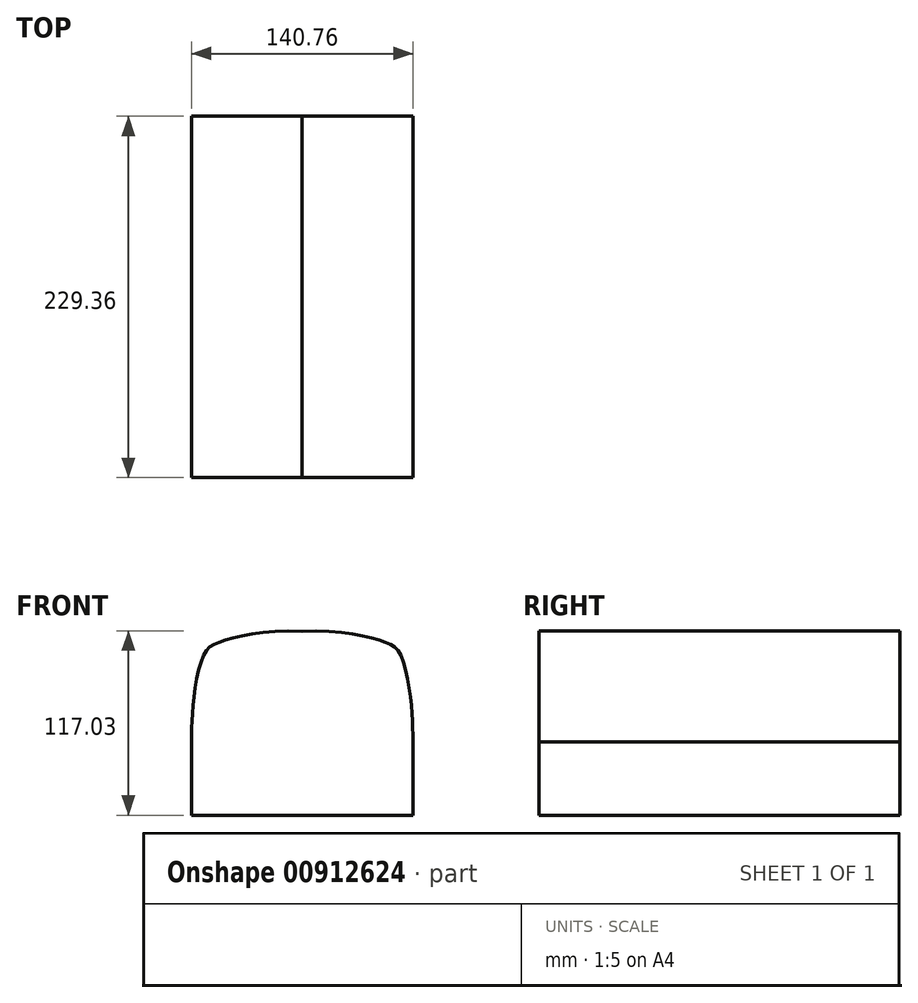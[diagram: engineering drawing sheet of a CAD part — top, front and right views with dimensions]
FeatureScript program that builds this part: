
annotation { "Feature Type Name" : "Feature", "Feature Type Description" : "" }
export const myFeature = defineFeature(function(context is Context, id is Id, definition is map)
    precondition{}
    {
        {
            var Q0;
            Q0=qCreatedBy(makeId("Front.planeOp"),FACE);
            var sketch = newSketch(context, id + "F0", { "sketchPlane" : qUnion([Q0])});
            skLineSegment(sketch, "E0", {"start": v(-70.38, -58.83) * mm, "end": v(70.38, -58.83) * mm});
            skLineSegment(sketch, "E1", {"start": v(70.38, -58.83) * mm, "end": v(70.38, -12.25) * mm});
            skLineSegment(sketch, "E2", {"start": v(-70.38, -58.83) * mm, "end": v(-70.38, -12.25) * mm});
            skFitSpline(sketch, "E3", {"points": [v(-70.38, -12.25) * mm, v(-69.1, 13) * mm, v(-61.82, 44.19) * mm, v(-51.98, 51.3) * mm, v(0, 57.92) * mm], "startDerivative": vector(3.91, 99.43) * mm, "endDerivative": vector(209.58, -13.11) * mm});
            skLineSegment(sketch, "E4", {"start": v(0, 57.92) * mm, "end": v(0, -58.83) * mm});
            skFitSpline(sketch, "E5.MirrorCS", {"points": [v(70.38, -12.25) * mm, v(69.1, 13) * mm, v(61.82, 44.19) * mm, v(51.98, 51.3) * mm, v(0, 57.92) * mm], "startDerivative": vector(-3.91, 99.43) * mm, "endDerivative": vector(-209.58, -13.11) * mm});
            skSolve(sketch);
        }
        {
            var Q0;
            Q0 = qSketchRegion(id + "F0", true);
            var Q1;
            Q1=sQuery(id+"F0.wireOp",EDGE,"E3");
            var Q2;
            Q2=sQuery(id+"F0.wireOp",EDGE,"E2");
            var Q3;
            Q3=sQuery(id+"F0.wireOp",EDGE,"E0");
            var Q4;
            Q4=sQuery(id+"F0.wireOp",EDGE,"E1");
            var Q5;
            Q5=sQuery(id+"F0.wireOp",EDGE,"E5.MirrorCS");
            extrude(context, id + "F1", {"entities" : qUnion([Q0]), "bodyType" : ToolBodyType.SURFACE, "surfaceEntities" : qUnion([Q1, Q2, Q3, Q4, Q5]), "oppositeDirection" : true, "depth" : 229.36 * mm, "offsetDistance" : 25.4 * mm});
        }
    });
